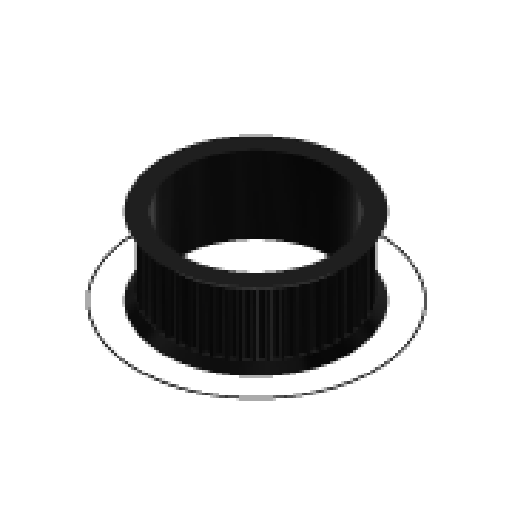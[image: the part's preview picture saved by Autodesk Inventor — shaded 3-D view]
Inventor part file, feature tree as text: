
AUTODESK INVENTOR PART (.ipt)
format: ipt  version: 2024.1 (Build 281209000, 209)  size: 283,648 bytes
history: native  units: mm
features: other x2, sketch x1
ambient origin geometry x8: Origin, YZ Plane, XZ Plane, XY Plane, X Axis, Y Axis, Z Axis, Center Point
feature tree (3):
  other  "00_gt2_pulley_53tooth"
  sketch  "Skizze1"
  other  "MeshFeature1"
